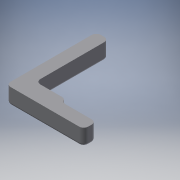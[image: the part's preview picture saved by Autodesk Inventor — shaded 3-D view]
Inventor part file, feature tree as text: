
AUTODESK INVENTOR PART (.ipt)
format: ipt  version: 2018 (Build 220112000, 112)  size: 191,488 bytes
history: native  units: mm
features: reference x17, other x4, extrude x2, sketch x2, fillet x1, projected_geometry x1
ambient origin geometry x8: Origin, YZ Plane, XZ Plane, XY Plane, X Axis, Y Axis, Z Axis, Center Point
bodies: Volumenkörper1 (feature_tree)
feature tree (27):
  extrude  "Extrusion1"  Depth=1.5mm
  fillet  "Rundung1"  Radius=2.0mm
  extrude  "Extrusion2"  Depth=5.0mm TaperAngle=0.0deg
  sketch  "Skizze1"  dims[d0=0.25mm d1=1.5mm d2=2.0mm]
  reference  "Referenz1"
  reference  "Referenz2"
  reference  "Referenz3"
  reference  "Referenz4"
  reference  "Referenz5"
  reference  "Referenz6"
  reference  "Referenz7"
  reference  "Referenz8"
  reference  "Referenz9"
  reference  "Referenz10"
  reference  "Referenz11"
  reference  "Referenz12"
  reference  "Referenz13"
  reference  "Referenz14"
  reference  "Referenz15"
  reference  "Referenz16"
  reference  "Referenz17"
  sketch  "Skizze2"  dims[d3=2.0mm d4=5.0mm d5=0.0mm d6=1.0mm d7=2.0mm d8=0.0mm]
  projected_geometry  "Projizierte Kontur1"
  parser-record x1  (decoder bookkeeping rows leaked as tree rows — omitted from the tree; the rows remain in map.json)
  other  "Montiert.iam"
  other  "Front:1"
  other  "Seite:1"
note: 1 file-system path scrubbed to <path> (originals preserved in map.json)
